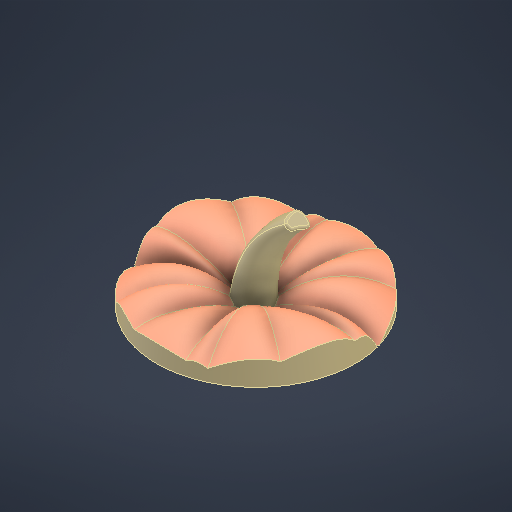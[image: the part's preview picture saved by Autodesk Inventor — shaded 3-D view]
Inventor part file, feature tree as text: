
AUTODESK INVENTOR PART (.ipt)
format: ipt  version: 2025.1 (Build 291241020, 241B)  size: 1,095,680 bytes
history: native  units: in
note: dims shown in document units (in); Inventor stores cm internally (conversion verified against a paired STEP export)
features: other x14, extrude x2, sketch x2
ambient origin geometry x8: Origin, YZ Plane, XZ Plane, XY Plane, X Axis, Y Axis, Z Axis, Center Point
bodies: Solid1 (feature_tree)
feature tree (18):
  other  "Axe1"
  other  "Plan1"
  other  "Plan2"
  other  "Plan3"
  other  "Plan4"
  other  "Plan5"
  other  "Plan6"
  other  "Plan7"
  other  "Plan8"
  other  "Plan9"
  other  "Plan10"
  other  "Plan11"
  other  "Plan12"
  extrude  "Extrusion1"  Depth=8.4562in TaperAngle=0.0deg
  extrude  "Extrusion2"  Depth=9.0551in
  sketch  "Sketch1"  dims[d0=7.874in d1=8.4562in d2=0.0in]
  sketch  "Sketch2"  dims[d3=7.0866in d4=9.0551in d5=0.2062in d6=1.5094in d7=0.0in d8=0.0in]
  other  "Enlèv. mat.-Extru.2"
